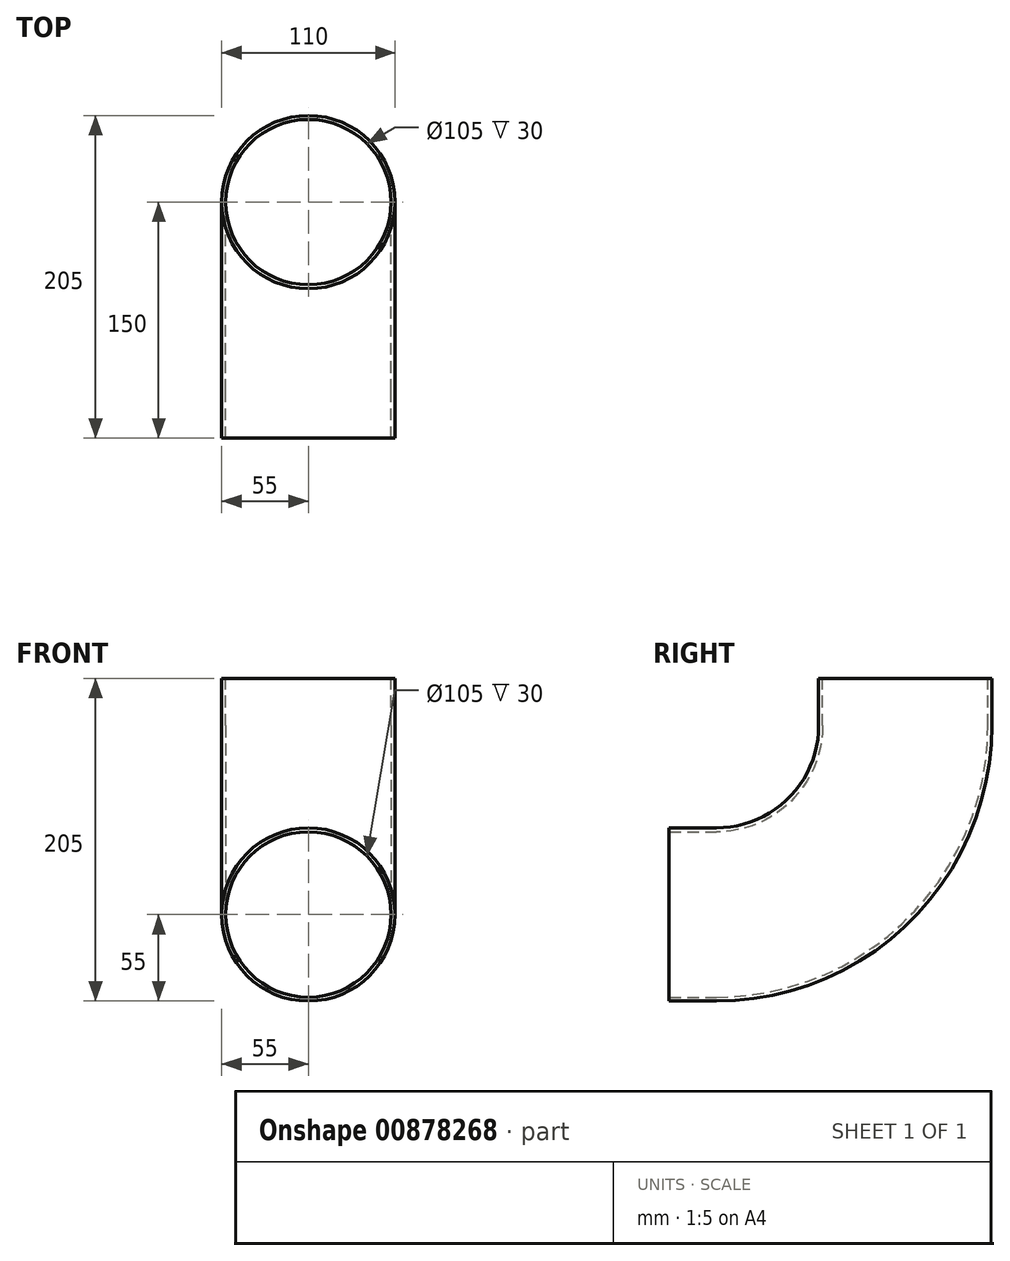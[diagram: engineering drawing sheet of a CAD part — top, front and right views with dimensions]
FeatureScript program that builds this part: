
annotation { "Feature Type Name" : "Feature", "Feature Type Description" : "" }
export const myFeature = defineFeature(function(context is Context, id is Id, definition is map)
    precondition{}
    {
        {
            var Q0;
            Q0=qCreatedBy(makeId("Front.planeOp"),FACE);
            var sketch = newSketch(context, id + "F0", { "sketchPlane" : qUnion([Q0])});
            skCircle(sketch, "E0", {"center": v(0, 0) * mm, "radius": 52.5 * mm});
            skCircle(sketch, "E1", {"center": v(0, 0) * mm, "radius": 55 * mm});
            skSolve(sketch);
        }
        {
            var Q0;
            Q0=qCreatedBy(makeId("Right.planeOp"),FACE);
            var sketch = newSketch(context, id + "F1", { "sketchPlane" : qUnion([Q0])});
            skLineSegment(sketch, "E2", {"start": v(0, 0) * mm, "end": v(30, 0) * mm});
            skLineSegment(sketch, "E3", {"start": v(150, 120) * mm, "end": v(150, 150) * mm});
            skPoint(sketch, "E4.visualSharp", {"position": v(150, 0) * mm});
            skArc(sketch, "E4.filletArc", {"start": v(30, 0) * mm, "mid": v(114.85, 35.15) * mm, "end": v(150, 120) * mm});
            skSolve(sketch);
        }
        {
            var Q0;
            Q0=makeQuery(id+"F0.imprint","IMPRINT",FACE,{"disambiguationData":[TD([[makeQuery(id+"F0.imprint","IMPRINT",EDGE,{"derivedFrom":sQuery(id+"F0.wireOp",EDGE,"E0")}),-1.0]])]});
            var Q1;
            Q1=sQuery(id+"F1.wireOp",EDGE,"E2");
            var Q2;
            Q2=sQuery(id+"F1.wireOp",EDGE,"E4.filletArc");
            var Q3;
            Q3=sQuery(id+"F1.wireOp",EDGE,"E3");
            sweep(context, id + "F2", {"profiles" : qUnion([Q0]), "path" : qUnion([Q1, Q2, Q3])});
        }
    });
